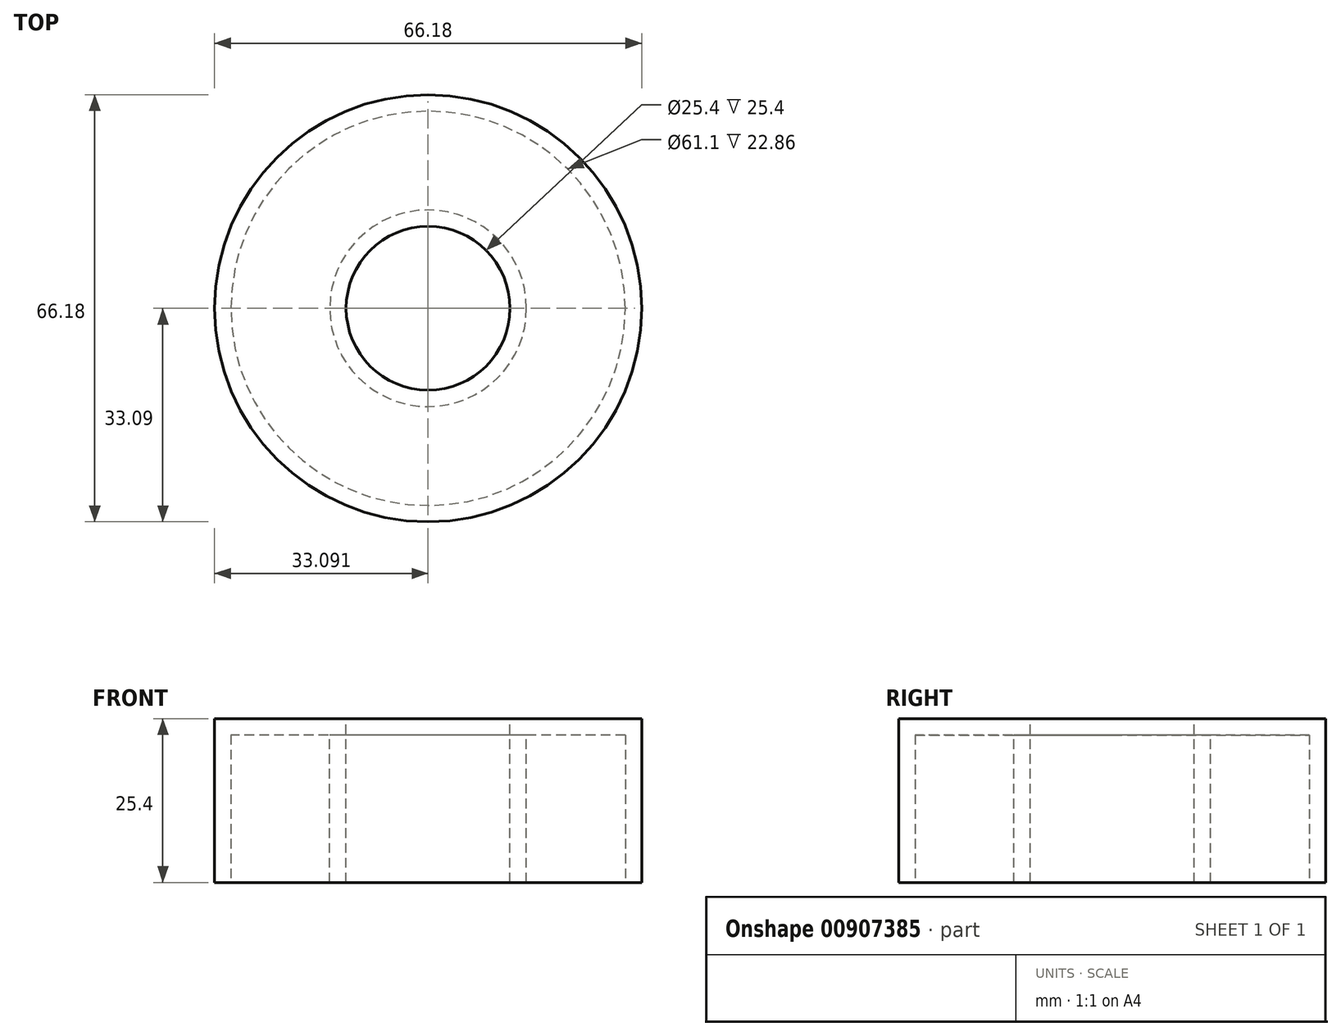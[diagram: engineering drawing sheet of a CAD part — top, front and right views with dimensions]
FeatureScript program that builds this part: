
annotation { "Feature Type Name" : "Feature", "Feature Type Description" : "" }
export const myFeature = defineFeature(function(context is Context, id is Id, definition is map)
    precondition{}
    {
        {
            var Q0;
            Q0=qCreatedBy(makeId("Top.planeOp"),FACE);
            var sketch = newSketch(context, id + "F0", { "sketchPlane" : qUnion([Q0])});
            skCircle(sketch, "E0", {"center": v(-2.02, 9.18) * mm, "radius": 33.1 * mm});
            skSolve(sketch);
        }
        {
            var Q0;
            Q0 = qSketchRegion(id + "F0", true);
            extrude(context, id + "F1", {"entities" : qUnion([Q0]), "depth" : 25.4 * mm, "offsetDistance" : 25.4 * mm});
        }
        {
            var Q0;
            Q0=makeQuery(id+"F1.opExtrude","CAP_FACE",FACE,{"disambiguationData":[OSD([sQuery(id+"F0.wireOp",EDGE,"E0")])],"isStart":false});
            var sketch = newSketch(context, id + "F2", { "sketchPlane" : qUnion([Q0])});
            skCircle(sketch, "E1", {"center": v(-2.02, 9.18) * mm, "radius": 12.7 * mm});
            skSolve(sketch);
        }
        {
            var Q0;
            Q0=sQuery(id+"F2.wireOp",VERTEX,"E1.center");
            var Q1;
            Q1=makeQuery(id+"F1.opExtrude","SWEPT_BODY",BODY,{"disambiguationData":[OSD([sQuery(id+"F0.wireOp",EDGE,"E0")])]});
            hole(context, id + "F3", {"style" : HoleStyle.SIMPLE, "endStyle" : HoleEndStyle.THROUGH, "holeDiameter" : 25.4 * mm, "majorDiameter" : 6.35 * mm, "isTappedThrough" : true, "tappedDepth" : 12.7 * mm, "tapClearance" : 3, "locations" : qUnion([Q0]), "scope" : qUnion([Q1])});
        }
        {
            var Q0;
            Q0=makeQuery(id+"F1.opExtrude","CAP_FACE",FACE,{"disambiguationData":[OSD([sQuery(id+"F0.wireOp",EDGE,"E0")])],"isStart":true});
            shell(context, id + "F4", {"entities" : qUnion([Q0]), "thickness" : 2.54 * mm});
        }
    });
